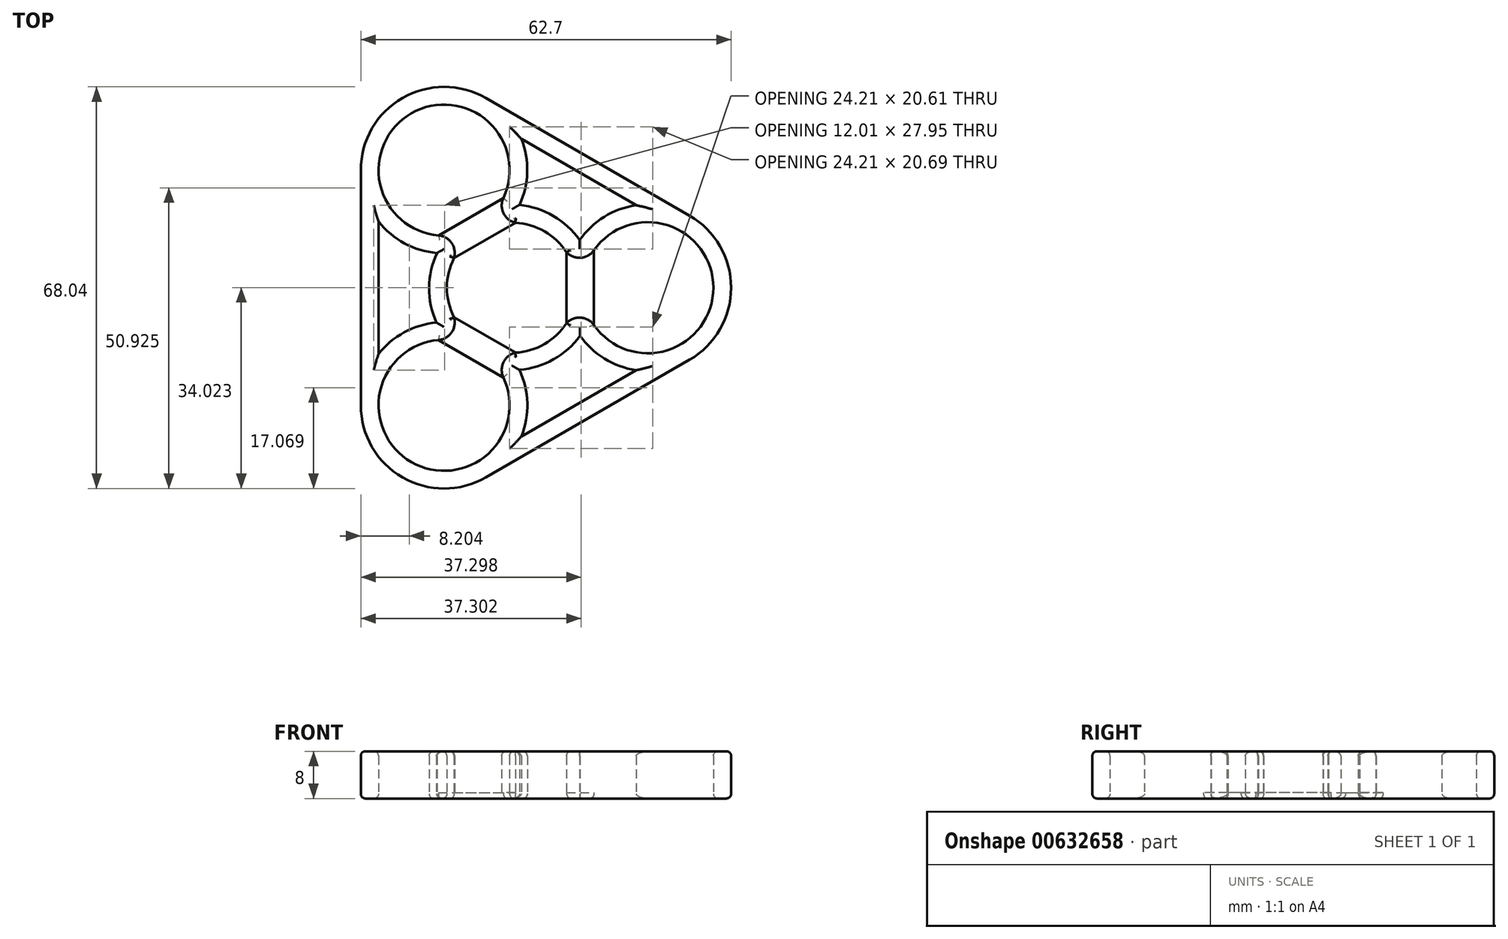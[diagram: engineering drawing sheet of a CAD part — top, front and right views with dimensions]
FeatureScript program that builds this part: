
annotation { "Feature Type Name" : "Feature", "Feature Type Description" : "" }
export const myFeature = defineFeature(function(context is Context, id is Id, definition is map)
    precondition{}
    {
        {
            var Q0;
            Q0=qCreatedBy(makeId("Top.planeOp"),FACE);
            var sketch = newSketch(context, id + "F0", { "sketchPlane" : qUnion([Q0])});
            skArc(sketch, "E0", {"start": v(9.25, 6) * mm, "mid": v(5.51, 9.55) * mm, "end": v(0.57, 11.01) * mm});
            skArc(sketch, "E1", {"start": v(13.9, -6.34) * mm, "mid": v(34.1, 0) * mm, "end": v(13.9, 6.34) * mm});
            skArc(sketch, "E2.0", {"start": v(1.28, 14.03) * mm, "mid": v(2.58, 19.58) * mm, "end": v(1.58, 25.18) * mm});
            skArc(sketch, "E3.0", {"start": v(11.46, -8.1) * mm, "mid": v(15.63, -12.02) * mm, "end": v(21.02, -13.96) * mm});
            skArc(sketch, "E4.trimOffspring", {"start": v(11.43, 8.06) * mm, "mid": v(7.01, 12.16) * mm, "end": v(1.28, 14.03) * mm});
            skLineSegment(sketch, "E5", {"start": v(-4.45, 32.13) * mm, "end": v(30.05, 12.21) * mm});
            skLineSegment(sketch, "E6.0", {"start": v(1.58, 25.18) * mm, "end": v(21.02, 13.96) * mm});
            skArc(sketch, "E7.trimOffspring", {"start": v(21.02, 13.96) * mm, "mid": v(15.61, 12) * mm, "end": v(11.43, 8.06) * mm});
            skArc(sketch, "E8", {"start": v(9.25, 6) * mm, "mid": v(11.65, 5.07) * mm, "end": v(13.9, 6.34) * mm});
            skLineSegment(sketch, "E9", {"start": v(0, 0) * mm, "end": v(23, 0) * mm, "construction": true});
            skArc(sketch, "E10.MirrorCS", {"start": v(9.25, -6) * mm, "mid": v(11.65, -5.07) * mm, "end": v(13.9, -6.34) * mm});
            skArc(sketch, "E11.1.0", {"start": v(-12.7, 5.87) * mm, "mid": v(-14.04, 0) * mm, "end": v(-12.8, -5.9) * mm});
            skLineSegment(sketch, "E11.1.1", {"start": v(-25.6, -19.92) * mm, "end": v(-25.6, 19.92) * mm});
            skArc(sketch, "E11.1.2", {"start": v(-12.8, -5.9) * mm, "mid": v(-18.25, -7.55) * mm, "end": v(-22.6, -11.22) * mm});
            skLineSegment(sketch, "E11.1.3", {"start": v(-22.6, -11.22) * mm, "end": v(-22.6, 11.22) * mm});
            skArc(sketch, "E11.1.4", {"start": v(-22.6, 11.22) * mm, "mid": v(-18.2, 7.51) * mm, "end": v(-12.7, 5.87) * mm});
            skArc(sketch, "E11.1.5", {"start": v(-9.82, 5.01) * mm, "mid": v(-10.22, 7.56) * mm, "end": v(-12.44, 8.86) * mm});
            skArc(sketch, "E11.1.6", {"start": v(-1.45, 15.2) * mm, "mid": v(-17.05, 29.53) * mm, "end": v(-12.44, 8.86) * mm});
            skArc(sketch, "E11.1.7", {"start": v(0.57, 11.01) * mm, "mid": v(-1.44, 12.63) * mm, "end": v(-1.45, 15.2) * mm});
            skArc(sketch, "E11.1.8", {"start": v(1.29, 13.97) * mm, "mid": v(2.6, 19.55) * mm, "end": v(1.58, 25.18) * mm});
            skArc(sketch, "E11.2.0", {"start": v(1.26, -13.93) * mm, "mid": v(7.02, -12.15) * mm, "end": v(11.51, -8.12) * mm});
            skLineSegment(sketch, "E11.2.1", {"start": v(30.05, -12.21) * mm, "end": v(-4.45, -32.13) * mm});
            skArc(sketch, "E11.2.2", {"start": v(11.51, -8.12) * mm, "mid": v(15.66, -12.03) * mm, "end": v(21.02, -13.96) * mm});
            skLineSegment(sketch, "E11.2.3", {"start": v(21.02, -13.96) * mm, "end": v(1.58, -25.18) * mm});
            skArc(sketch, "E11.2.4", {"start": v(1.58, -25.18) * mm, "mid": v(2.6, -19.52) * mm, "end": v(1.26, -13.93) * mm});
            skArc(sketch, "E11.2.5", {"start": v(0.57, -11.01) * mm, "mid": v(-1.44, -12.63) * mm, "end": v(-1.45, -15.2) * mm});
            skArc(sketch, "E11.2.6", {"start": v(-12.44, -8.86) * mm, "mid": v(-17.05, -29.53) * mm, "end": v(-1.45, -15.2) * mm});
            skArc(sketch, "E11.2.7", {"start": v(-9.82, -5.01) * mm, "mid": v(-10.22, -7.56) * mm, "end": v(-12.44, -8.86) * mm});
            skArc(sketch, "E11.2.8", {"start": v(-12.74, -5.87) * mm, "mid": v(-18.23, -7.53) * mm, "end": v(-22.6, -11.22) * mm});
            skArc(sketch, "E12.trimOffspring", {"start": v(0.57, -11.01) * mm, "mid": v(5.51, -9.55) * mm, "end": v(9.25, -6) * mm});
            skArc(sketch, "E13.trimOffspring", {"start": v(-9.82, 5.01) * mm, "mid": v(-11.03, 0) * mm, "end": v(-9.82, -5.01) * mm});
            skArc(sketch, "E14.trimOffspring", {"start": v(-4.45, 32.13) * mm, "mid": v(-18.55, 32.13) * mm, "end": v(-25.6, 19.92) * mm});
            skArc(sketch, "E15.trimOffspring", {"start": v(-25.6, -19.92) * mm, "mid": v(-18.55, -32.13) * mm, "end": v(-4.45, -32.13) * mm});
            skArc(sketch, "E16.trimOffspring", {"start": v(30.05, -12.21) * mm, "mid": v(37.1, 0) * mm, "end": v(30.05, 12.21) * mm});
            skLineSegment(sketch, "E17", {"start": v(-12.44, 8.86) * mm, "end": v(-1.45, 15.2) * mm});
            skLineSegment(sketch, "E18", {"start": v(-9.82, 5.01) * mm, "end": v(0.57, 11.01) * mm});
            skLineSegment(sketch, "E19", {"start": v(13.9, 6.34) * mm, "end": v(13.9, -6.34) * mm});
            skLineSegment(sketch, "E20", {"start": v(9.25, 6) * mm, "end": v(9.25, -6) * mm});
            skLineSegment(sketch, "E21", {"start": v(-9.82, -5.01) * mm, "end": v(0.57, -11.01) * mm});
            skLineSegment(sketch, "E22", {"start": v(-12.44, -8.86) * mm, "end": v(-1.45, -15.2) * mm});
            skSolve(sketch);
        }
        {
            var Q0;
            Q0=makeQuery(id+"F0.imprint","IMPRINT",FACE,{"disambiguationData":[TD([[makeQuery(id+"F0.imprint","IMPRINT",EDGE,{"derivedFrom":sQuery(id+"F0.wireOp",EDGE,"E0")}),-1.0]])]});
            extrude(context, id + "F1", {"entities" : qUnion([Q0]), "depth" : 8 * mm, "offsetDistance" : 25.4 * mm});
        }
        {
            var Q0;
            Q0=makeQuery(id+"F0.imprint","IMPRINT",FACE,{"disambiguationData":[TD([[makeQuery(id+"F0.imprint","IMPRINT",EDGE,{"derivedFrom":sQuery(id+"F0.wireOp",EDGE,"E8")}),-1.0]])]});
            var Q1;
            Q1=makeQuery(id+"F0.imprint","IMPRINT",FACE,{"disambiguationData":[TD([[makeQuery(id+"F0.imprint","IMPRINT",EDGE,{"derivedFrom":sQuery(id+"F0.wireOp",EDGE,"E11.1.5")}),-1.0]])]});
            var Q2;
            Q2=makeQuery(id+"F0.imprint","IMPRINT",FACE,{"disambiguationData":[TD([[makeQuery(id+"F0.imprint","IMPRINT",EDGE,{"derivedFrom":sQuery(id+"F0.wireOp",EDGE,"E11.2.5")}),-1.0]])]});
            extrude(context, id + "F2", {"entities" : qUnion([Q0, Q1, Q2]), "operationType" : NewBodyOperationType.ADD, "depth" : 1 * mm, "offsetDistance" : 25 * mm});
        }
        {
            var Q0;
            Q0=makeQuery(id+"F1.opExtrude","CAP_FACE",FACE,{"disambiguationData":[OSD([sQuery(id+"F0.wireOp",EDGE,"E0"),sQuery(id+"F0.wireOp",EDGE,"E1"),sQuery(id+"F0.wireOp",EDGE,"E2.0"),sQuery(id+"F0.wireOp",EDGE,"E4.trimOffspring"),sQuery(id+"F0.wireOp",EDGE,"E5"),sQuery(id+"F0.wireOp",EDGE,"E6.0"),sQuery(id+"F0.wireOp",EDGE,"E7.trimOffspring"),sQuery(id+"F0.wireOp",EDGE,"E8"),sQuery(id+"F0.wireOp",EDGE,"E10.MirrorCS"),sQuery(id+"F0.wireOp",EDGE,"E11.1.0"),sQuery(id+"F0.wireOp",EDGE,"E11.1.1"),sQuery(id+"F0.wireOp",EDGE,"E11.1.2"),sQuery(id+"F0.wireOp",EDGE,"E11.1.3"),sQuery(id+"F0.wireOp",EDGE,"E11.1.4"),sQuery(id+"F0.wireOp",EDGE,"E11.1.5"),sQuery(id+"F0.wireOp",EDGE,"E11.1.6"),sQuery(id+"F0.wireOp",EDGE,"E11.1.7"),sQuery(id+"F0.wireOp",EDGE,"E11.2.0"),sQuery(id+"F0.wireOp",EDGE,"E11.2.1"),sQuery(id+"F0.wireOp",EDGE,"E11.2.2"),sQuery(id+"F0.wireOp",EDGE,"E11.2.3"),sQuery(id+"F0.wireOp",EDGE,"E11.2.4"),sQuery(id+"F0.wireOp",EDGE,"E11.2.5"),sQuery(id+"F0.wireOp",EDGE,"E11.2.6"),sQuery(id+"F0.wireOp",EDGE,"E11.2.7"),sQuery(id+"F0.wireOp",EDGE,"E12.trimOffspring"),sQuery(id+"F0.wireOp",EDGE,"E13.trimOffspring"),sQuery(id+"F0.wireOp",EDGE,"E14.trimOffspring"),sQuery(id+"F0.wireOp",EDGE,"E15.trimOffspring"),sQuery(id+"F0.wireOp",EDGE,"E16.trimOffspring")])],"isStart":false});
            var Q1;
            {var subQ0=sQuery(id+"F0.wireOp",EDGE,"E11.2.7");var subQ1=sQuery(id+"F0.wireOp",EDGE,"E11.2.5");var subQ2=sQuery(id+"F0.wireOp",EDGE,"E11.1.7");var subQ3=sQuery(id+"F0.wireOp",EDGE,"E11.1.5");var subQ4=sQuery(id+"F0.wireOp",EDGE,"E10.MirrorCS");var subQ5=sQuery(id+"F0.wireOp",EDGE,"E8");Q1=makeQuery(id+"F2.boolean.opBoolean","MERGE",FACE,{"derivedFrom":[makeQuery(id+"F1.opExtrude","CAP_FACE",FACE,{"disambiguationData":[OSD([sQuery(id+"F0.wireOp",EDGE,"E0"),sQuery(id+"F0.wireOp",EDGE,"E1"),sQuery(id+"F0.wireOp",EDGE,"E2.0"),sQuery(id+"F0.wireOp",EDGE,"E4.trimOffspring"),sQuery(id+"F0.wireOp",EDGE,"E5"),sQuery(id+"F0.wireOp",EDGE,"E6.0"),sQuery(id+"F0.wireOp",EDGE,"E7.trimOffspring"),subQ5,subQ4,sQuery(id+"F0.wireOp",EDGE,"E11.1.0"),sQuery(id+"F0.wireOp",EDGE,"E11.1.1"),sQuery(id+"F0.wireOp",EDGE,"E11.1.2"),sQuery(id+"F0.wireOp",EDGE,"E11.1.3"),sQuery(id+"F0.wireOp",EDGE,"E11.1.4"),subQ3,sQuery(id+"F0.wireOp",EDGE,"E11.1.6"),subQ2,sQuery(id+"F0.wireOp",EDGE,"E11.2.0"),sQuery(id+"F0.wireOp",EDGE,"E11.2.1"),sQuery(id+"F0.wireOp",EDGE,"E11.2.2"),sQuery(id+"F0.wireOp",EDGE,"E11.2.3"),sQuery(id+"F0.wireOp",EDGE,"E11.2.4"),subQ1,sQuery(id+"F0.wireOp",EDGE,"E11.2.6"),subQ0,sQuery(id+"F0.wireOp",EDGE,"E12.trimOffspring"),sQuery(id+"F0.wireOp",EDGE,"E13.trimOffspring"),sQuery(id+"F0.wireOp",EDGE,"E14.trimOffspring"),sQuery(id+"F0.wireOp",EDGE,"E15.trimOffspring"),sQuery(id+"F0.wireOp",EDGE,"E16.trimOffspring")])],"isStart":true}),makeQuery(id+"F2.opExtrude","CAP_FACE",FACE,{"disambiguationData":[OSD([subQ5,subQ4,sQuery(id+"F0.wireOp",EDGE,"E19"),sQuery(id+"F0.wireOp",EDGE,"E20")])],"isStart":true}),makeQuery(id+"F2.opExtrude","CAP_FACE",FACE,{"disambiguationData":[OSD([subQ3,subQ2,sQuery(id+"F0.wireOp",EDGE,"E17"),sQuery(id+"F0.wireOp",EDGE,"E18")])],"isStart":true}),makeQuery(id+"F2.opExtrude","CAP_FACE",FACE,{"disambiguationData":[OSD([subQ1,subQ0,sQuery(id+"F0.wireOp",EDGE,"E21"),sQuery(id+"F0.wireOp",EDGE,"E22")])],"isStart":true})]});}
            fillet(context, id + "F3", {"entities" : qUnion([Q0, Q1]), "radius" : .8 * mm, "tangentPropagation" : true, "allowEdgeOverflow" : false});
        }
    });
